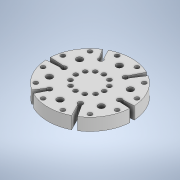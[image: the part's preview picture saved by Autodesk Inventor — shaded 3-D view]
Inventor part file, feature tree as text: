
AUTODESK INVENTOR PART (.ipt)
format: ipt  version: 2021 (Build 250183000, 183)  size: 219,136 bytes
history: native  units: mm
features: extrude x1, sketch x1
ambient origin geometry x8: Origin, YZ Plane, XZ Plane, XY Plane, X Axis, Y Axis, Z Axis, Center Point
bodies: Solid1 (feature_tree)
feature tree (2):
  extrude  "Extrusion1"  Depth=10.0mm
  sketch  "Sketch1"  dims[d1=60.0deg d2=15.0deg d3=15.0deg d4=62.0mm d7=48.0mm d9=15.0deg d10=23.0mm d12=0.523599mm d13=0.523599mm d14=42.0mm d15=4.0mm d19=10.0mm d20=0.0mm]
